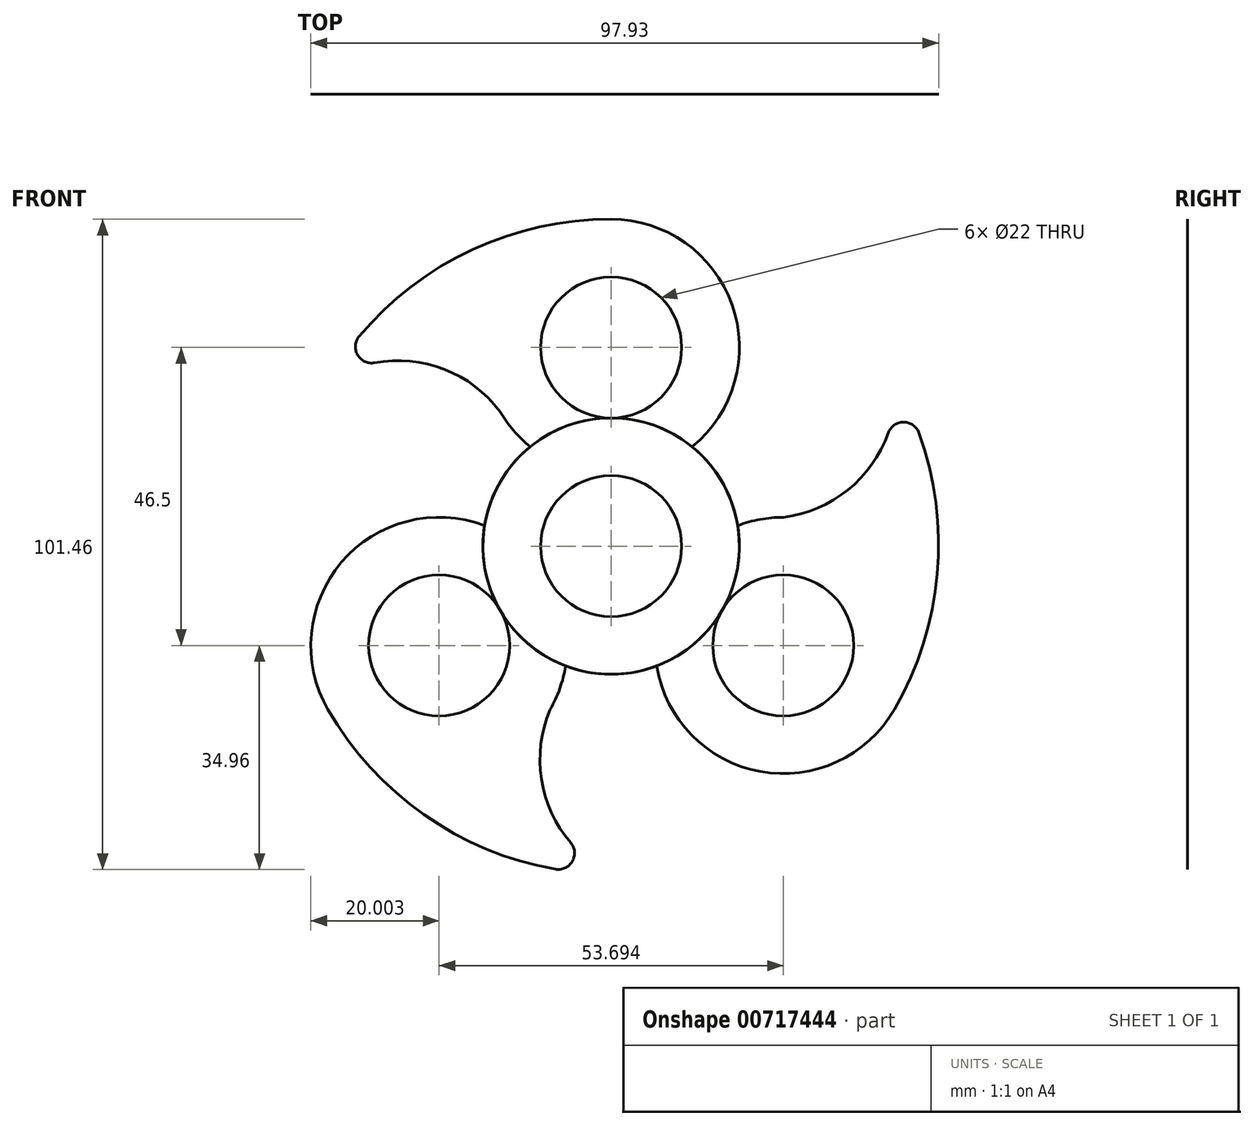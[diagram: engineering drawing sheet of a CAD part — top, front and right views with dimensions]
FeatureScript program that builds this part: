
annotation { "Feature Type Name" : "Feature", "Feature Type Description" : "" }
export const myFeature = defineFeature(function(context is Context, id is Id, definition is map)
    precondition{}
    {
        {
            assignVariable(context, id + "F0", {"name" : "thick", "anyValue" : 1 / 101.6 * mm});
        }
        {
            var Q0;
            Q0=qCreatedBy(makeId("Front.planeOp"),FACE);
            var sketch = newSketch(context, id + "F1", { "sketchPlane" : qUnion([Q0])});
            skCircle(sketch, "E0", {"center": v(0, 0) * mm, "radius": 11 * mm});
            skArc(sketch, "E1", {"start": v(-12.64, 15.5) * mm, "mid": v(0, -20) * mm, "end": v(12.64, 15.5) * mm});
            skCircle(sketch, "E2", {"center": v(0, 31) * mm, "radius": 11 * mm});
            skArc(sketch, "E3", {"start": v(12.64, 15.5) * mm, "mid": v(0, 51) * mm, "end": v(-12.64, 15.5) * mm});
            skLineSegment(sketch, "E4", {"start": v(0, 0) * mm, "end": v(0, 51) * mm, "construction": true});
            skLineSegment(sketch, "E5", {"start": v(0, 0) * mm, "end": v(-44.34, 25.6) * mm, "construction": true});
            skLineSegment(sketch, "E6", {"start": v(0, 31) * mm, "end": v(-17.32, 21) * mm, "construction": true});
            skArc(sketch, "E7", {"start": v(0, 51) * mm, "mid": v(-21.68, 46.24) * mm, "end": v(-39.31, 32.74) * mm});
            skArc(sketch, "E8", {"start": v(-17.32, 21) * mm, "mid": v(-26.03, 27.58) * mm, "end": v(-36.9, 28.6) * mm});
            skPoint(sketch, "E9.visualSharp", {"position": v(-44.34, 25.6) * mm});
            skArc(sketch, "E9.filletArc", {"start": v(-39.31, 32.74) * mm, "mid": v(-39.56, 29.83) * mm, "end": v(-36.9, 28.6) * mm});
            skSolve(sketch);
        }
        {
            var Q0;
            Q0=makeQuery(id+"F1.imprint","IMPRINT",FACE,{"disambiguationData":[TD([[makeQuery(id+"F1.imprint","IMPRINT",EDGE,{"derivedFrom":sQuery(id+"F1.wireOp",EDGE,"E0")}),-1.0]])]});
            var Q1;
            {var subQ0=sQuery(id+"F1.wireOp",EDGE,"RWrqEByo-HKUn-tdvG-MY4w-aMGRT2jewm6U");Q1=makeQuery(id+"F1.imprint","IMPRINT",FACE,{"disambiguationData":[TD([[makeQuery(id+"F1.imprint","IMPRINT",EDGE,{"derivedFrom":subQ0}),1.0]])]});}
            var Q2;
            {var subQ3=sQuery(id+"F1.wireOp",EDGE,"SXBKytdi-oU9p-iFW1-mU31-lHk7lJGYXJUD");Q2=makeQuery(id+"F1.imprint","IMPRINT",FACE,{"disambiguationData":[TD([[makeQuery(id+"F1.imprint","IMPRINT",EDGE,{"derivedFrom":subQ3}),-1.0]])]});}
            var Q3;
            {var subQ3=sQuery(id+"F1.wireOp",EDGE,"Vd1vkfKw-dstG-xjpd-db2K-r6FYEbVVuGfL");Q3=makeQuery(id+"F1.imprint","IMPRINT",FACE,{"disambiguationData":[TD([[makeQuery(id+"F1.imprint","IMPRINT",EDGE,{"derivedFrom":subQ3}),-1.0]])]});}
            var Q4;
            {var subQ0=sQuery(id+"F1.wireOp",EDGE,"E3");var subQ1=sQuery(id+"F1.wireOp",EDGE,"E1");var subQ2=makeQuery(id+"F1.imprint","INTERSECT",VERTEX,{"disambiguationData":[OD(0.0)],"derivedFrom":[subQ1,subQ0]});Q4=makeQuery(id+"F1.imprint","IMPRINT",FACE,{"disambiguationData":[TD([[makeQuery(id+"F1.imprint","IMPRINT",EDGE,{"disambiguationData":[TD([[subQ2,-1.0]])],"derivedFrom":subQ1}),-1.0]])]});}
            var Q5;
            {var subQ0=sQuery(id+"F1.wireOp",EDGE,"E3");var subQ1=sQuery(id+"F1.wireOp",EDGE,"E1");var subQ2=makeQuery(id+"F1.imprint","INTERSECT",VERTEX,{"disambiguationData":[OD(1.0)],"derivedFrom":[subQ1,subQ0]});Q5=makeQuery(id+"F1.imprint","IMPRINT",FACE,{"disambiguationData":[TD([[makeQuery(id+"F1.imprint","IMPRINT",EDGE,{"disambiguationData":[TD([[subQ2,1.0]])],"derivedFrom":subQ1}),-1.0]])]});}
            var Q6;
            {var subQ0=sQuery(id+"F1.wireOp",EDGE,"E7");Q6=makeQuery(id+"F1.imprint","IMPRINT",FACE,{"disambiguationData":[TD([[makeQuery(id+"F1.imprint","IMPRINT",EDGE,{"derivedFrom":subQ0}),1.0]])]});}
            extrude(context, id + "F2", {"entities" : qUnion([Q0, Q1, Q2, Q3, Q4, Q5, Q6]), "endBound" : BoundingType.SYMMETRIC, "depth" : getVariable(context, 'thick'), "offsetDistance" : 25.4 * mm});
        }
        {
            var Q0;
            Q0=makeQuery(id+"F2.opExtrude","SWEPT_BODY",BODY,{"disambiguationData":[OSD([sQuery(id+"F1.wireOp",EDGE,"E0"),sQuery(id+"F1.wireOp",EDGE,"E1"),sQuery(id+"F1.wireOp",EDGE,"E2"),sQuery(id+"F1.wireOp",EDGE,"E3")])]});
            var Q1;
            Q1=makeQuery(id+"F2.opExtrude","CAP_EDGE",EDGE,{"disambiguationData":[OSD([sQuery(id+"F1.wireOp",EDGE,"E0")])],"isStart":false});
            circularPattern(context, id + "F3", {"entities" : qUnion([Q0]), "axis" : qUnion([Q1]), "angle" : 360 * degree, "instanceCount" : 3, "equalSpace" : true});
        }
    });
